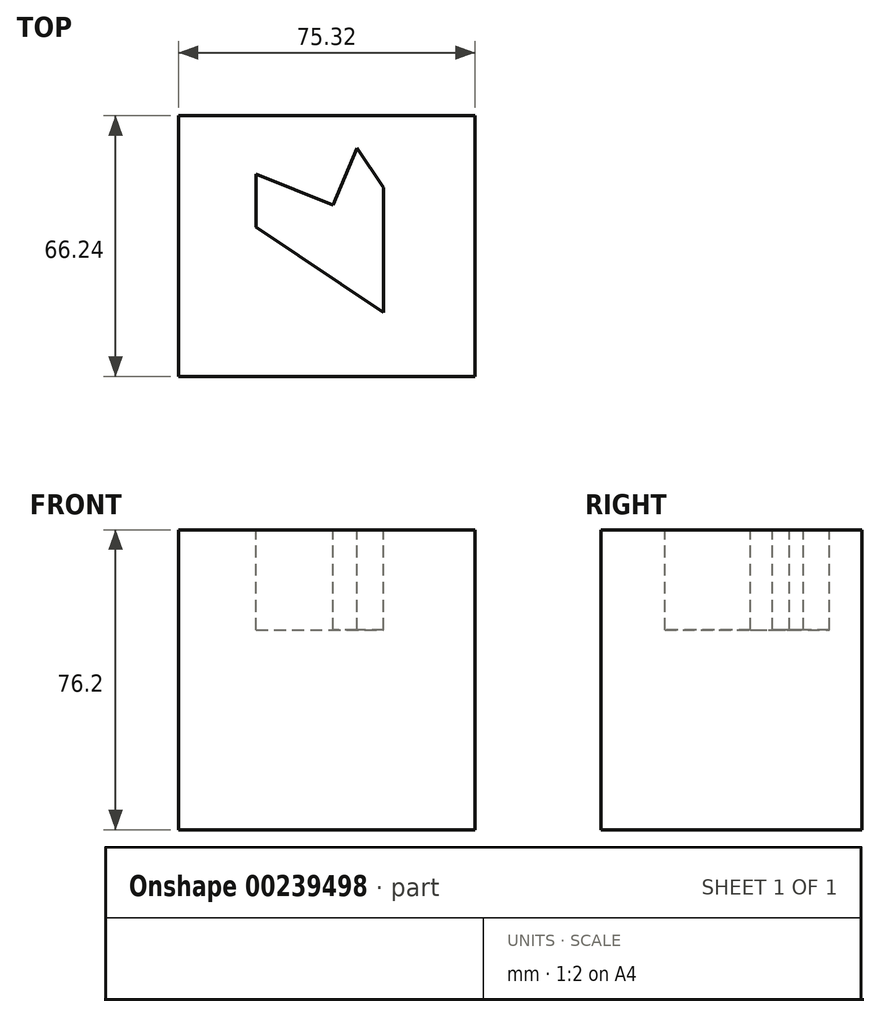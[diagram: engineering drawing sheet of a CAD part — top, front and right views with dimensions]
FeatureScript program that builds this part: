
annotation { "Feature Type Name" : "Feature", "Feature Type Description" : "" }
export const myFeature = defineFeature(function(context is Context, id is Id, definition is map)
    precondition{}
    {
        {
            var Q0;
            Q0=qCreatedBy(makeId("Top.planeOp"),FACE);
            var sketch = newSketch(context, id + "F0", { "sketchPlane" : qUnion([Q0])});
            skLineSegment(sketch, "E0.bottom", {"start": v(37.66, 33.12) * mm, "end": v(-37.66, 33.12) * mm});
            skLineSegment(sketch, "E0.top", {"start": v(37.66, -33.12) * mm, "end": v(-37.66, -33.12) * mm});
            skLineSegment(sketch, "E0.left", {"start": v(37.66, 33.12) * mm, "end": v(37.66, -33.12) * mm});
            skLineSegment(sketch, "E0.right", {"start": v(-37.66, 33.12) * mm, "end": v(-37.66, -33.12) * mm});
            skPoint(sketch, "E0.middle", {"position": v(0, 0) * mm});
            skSolve(sketch);
        }
        {
            var Q0;
            Q0 = qSketchRegion(id + "F0", true);
            extrude(context, id + "F1", {"entities" : qUnion([Q0]), "endBound" : BoundingType.SYMMETRIC, "depth" : 76.2 * mm});
        }
        {
            var Q0;
            Q0=makeQuery(id+"F1.opExtrude","CAP_FACE",FACE,{"disambiguationData":[OSD([sQuery(id+"F0.wireOp",EDGE,"E0.bottom"),sQuery(id+"F0.wireOp",EDGE,"E0.top"),sQuery(id+"F0.wireOp",EDGE,"E0.left"),sQuery(id+"F0.wireOp",EDGE,"E0.right")])],"isStart":false});
            var sketch = newSketch(context, id + "F2", { "sketchPlane" : qUnion([Q0])});
            skLineSegment(sketch, "E1", {"start": v(-17.95, 4.88) * mm, "end": v(14.47, -16.9) * mm});
            skLineSegment(sketch, "E2", {"start": v(14.47, -16.9) * mm, "end": v(14.47, 14.82) * mm});
            skLineSegment(sketch, "E3", {"start": v(-17.95, 4.88) * mm, "end": v(-17.95, 18.3) * mm});
            skLineSegment(sketch, "E4", {"start": v(-17.95, 18.3) * mm, "end": v(1.57, 10.46) * mm});
            skLineSegment(sketch, "E5", {"start": v(14.47, 14.82) * mm, "end": v(7.67, 24.92) * mm});
            skLineSegment(sketch, "E6", {"start": v(7.67, 24.92) * mm, "end": v(1.57, 10.46) * mm});
            skSolve(sketch);
        }
        {
            var Q0;
            Q0=makeQuery(id+"F2.imprint","IMPRINT",FACE,{"disambiguationData":[TD([[makeQuery(id+"F2.imprint","IMPRINT",EDGE,{"derivedFrom":sQuery(id+"F2.wireOp",EDGE,"E1")}),1.0]])]});
            extrude(context, id + "F3", {"entities" : qUnion([Q0]), "operationType" : NewBodyOperationType.REMOVE, "oppositeDirection" : true, "depth" : 25.4 * mm});
        }
    });
